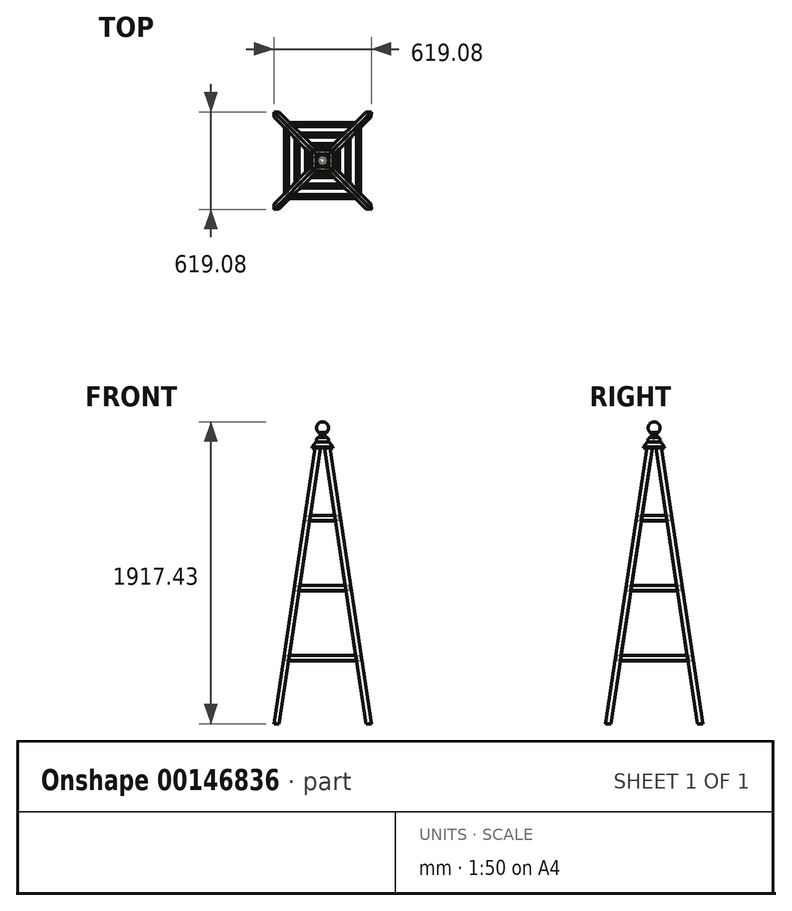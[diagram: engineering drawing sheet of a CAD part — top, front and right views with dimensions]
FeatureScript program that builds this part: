
annotation { "Feature Type Name" : "Feature", "Feature Type Description" : "" }
export const myFeature = defineFeature(function(context is Context, id is Id, definition is map)
    precondition{}
    {
        {
            assignVariable(context, id + "F0", {"name" : "Angle0", "anyValue" : 12 * degree});
        }
        {
            assignVariable(context, id + "F1", {"name" : "CentreSpread0", "anyValue" : 12});
        }
        {
            assignVariable(context, id + "F2", {"name" : "ArmOffset0", "anyValue" : ((((1800 - (sqrt(34 * 34 * 2) * sin(getVariable(context, 'Angle0')))) * sin(getVariable(context, 'Angle0')) + (sqrt(17 * 17 * 2) / cos(getVariable(context, 'Angle0')))) * sin(45 * degree)) + getVariable(context, 'CentreSpread0')) * mm});
        }
        {
            var Q0;
            Q0=qCreatedBy(makeId("Front.planeOp"),FACE);
            var sketch = newSketch(context, id + "F3", { "sketchPlane" : qUnion([Q0])});
            skLineSegment(sketch, "E0.bottom", {"start": v(-17, 900) * mm, "end": v(17, 900) * mm});
            skLineSegment(sketch, "E0.top", {"start": v(-17, -900) * mm, "end": v(17, -900) * mm});
            skLineSegment(sketch, "E0.left", {"start": v(-17, 900) * mm, "end": v(-17, -900) * mm});
            skLineSegment(sketch, "E0.right", {"start": v(17, 900) * mm, "end": v(17, -900) * mm});
            skPoint(sketch, "E0.middle", {"position": v(0, 0) * mm});
            skLineSegment(sketch, "E1", {"start": v(0, 0) * mm, "end": v(0, 406.37) * mm, "construction": true});
            skSolve(sketch);
        }
        {
            var Q0;
            Q0=sQuery(id+"F3.wireOp",EDGE,"E1");
            cPlane(context, id + "F4", {"entities" : qUnion([Q0]), "cplaneType" : CPlaneType.LINE_ANGLE, "offset" : 25 * mm, "angle" : 45 * degree, "width" : 150 * mm, "height" : 150 * mm});
        }
        {
            var Q0;
            Q0=sQuery(id+"F3.wireOp",EDGE,"E1");
            cPlane(context, id + "F5", {"entities" : qUnion([Q0]), "cplaneType" : CPlaneType.LINE_ANGLE, "offset" : 25 * mm, "angle" : 135 * degree, "width" : 150 * mm, "height" : 150 * mm});
        }
        {
            var Q0;
            Q0=qCreatedBy(id+"F5.planeOp",FACE);
            cPlane(context, id + "F6", {"entities" : qUnion([Q0]), "cplaneType" : CPlaneType.OFFSET, "offset" : (sqrt(17 * 17 * 2)) * mm, "oppositeDirection" : true, "width" : 150 * mm, "height" : 150 * mm});
        }
        {
            var Q0;
            Q0=qSketchRegion(id+"F3",true);
            extrude(context, id + "F7", {"entities" : qUnion([Q0]), "depth" : 17 * mm, "hasSecondDirection" : true, "secondDirectionOppositeDirection" : true, "secondDirectionDepth" : 17 * mm});
        }
        {
            var Q0;
            Q0=qCreatedBy(id+"F4.planeOp",FACE);
            var sketch = newSketch(context, id + "F8", { "sketchPlane" : qUnion([Q0])});
            skLineSegment(sketch, "E2", {"start": v(24.04, 900) * mm, "end": v(-24.04, 889.78) * mm});
            skLineSegment(sketch, "E3", {"start": v(-24.04, 900) * mm, "end": v(24.04, 900) * mm});
            skLineSegment(sketch, "E4", {"start": v(-24.04, 900) * mm, "end": v(-24.04, 889.78) * mm});
            skLineSegment(sketch, "E5", {"start": v(-24.04, -900) * mm, "end": v(24.04, -889.78) * mm});
            skLineSegment(sketch, "E6", {"start": v(-24.04, -900) * mm, "end": v(24.04, -900) * mm});
            skLineSegment(sketch, "E7", {"start": v(24.04, -900) * mm, "end": v(24.04, -889.78) * mm});
            skSolve(sketch);
        }
        {
            var Q0;
            Q0=qSketchRegion(id+"F8",true);
            extrude(context, id + "F9", {"entities" : qUnion([Q0]), "operationType" : NewBodyOperationType.REMOVE, "depth" : (sqrt(17 * 17 * 2)) * mm, "hasSecondDirection" : true, "secondDirectionOppositeDirection" : true, "secondDirectionDepth" : (sqrt(17 * 17 * 2)) * mm});
        }
        {
            var Q0;
            Q0=qCreatedBy(id+"F6.planeOp",FACE);
            var sketch = newSketch(context, id + "F10", { "sketchPlane" : qUnion([Q0])});
            skLineSegment(sketch, "E8", {"start": v(-24.04, -900) * mm, "end": v(24.04, -900) * mm, "construction": true});
            skSolve(sketch);
        }
        {
            var Q0;
            Q0=makeQuery(id+"F7.opExtrude","SWEPT_BODY",BODY,{"disambiguationData":[OSD([sQuery(id+"F3.wireOp",EDGE,"E0.bottom"),sQuery(id+"F3.wireOp",EDGE,"E0.top"),sQuery(id+"F3.wireOp",EDGE,"E0.left"),sQuery(id+"F3.wireOp",EDGE,"E0.right")])]});
            var Q1;
            Q1=sQuery(id+"F10.wireOp",EDGE,"E8");
            transform(context, id + "F11", {"entities" : qUnion([Q0]), "transformType" : TransformType.ROTATION, "transformAxis" : qUnion([Q1]), "angle" : getVariable(context, 'Angle0'), "makeCopy" : false});
        }
        {
            var Q0;
            Q0=makeQuery(id+"F7.opExtrude","SWEPT_BODY",BODY,{"disambiguationData":[OSD([sQuery(id+"F3.wireOp",EDGE,"E0.bottom"),sQuery(id+"F3.wireOp",EDGE,"E0.top"),sQuery(id+"F3.wireOp",EDGE,"E0.left"),sQuery(id+"F3.wireOp",EDGE,"E0.right")])]});
            transform(context, id + "F12", {"entities" : qUnion([Q0]), "transformType" : TransformType.TRANSLATION_3D, "dx" : getVariable(context, 'ArmOffset0'), "dy" : -getVariable(context, 'ArmOffset0'), "dz" : 0 * mm, "makeCopy" : false});
        }
        {
            var Q0;
            Q0=makeQuery(id+"F7.opExtrude","SWEPT_BODY",BODY,{"disambiguationData":[OSD([sQuery(id+"F3.wireOp",EDGE,"E0.bottom"),sQuery(id+"F3.wireOp",EDGE,"E0.top"),sQuery(id+"F3.wireOp",EDGE,"E0.left"),sQuery(id+"F3.wireOp",EDGE,"E0.right")])]});
            var Q1;
            Q1=sQuery(id+"F3.wireOp",EDGE,"E1");
            circularPattern(context, id + "F13", {"entities" : qUnion([Q0]), "axis" : qUnion([Q1]), "angle" : 360 * degree, "instanceCount" : 4, "equalSpace" : true});
        }
        {
            var Q0;
            Q0=qCreatedBy(makeId("Top.planeOp"),FACE);
            var sketch = newSketch(context, id + "F14", { "sketchPlane" : qUnion([Q0])});
            skLineSegment(sketch, "E9.bottom", {"start": v(67, 67) * mm, "end": v(-67, 67) * mm});
            skLineSegment(sketch, "E9.top", {"start": v(67, -67) * mm, "end": v(-67, -67) * mm});
            skLineSegment(sketch, "E9.left", {"start": v(67, 67) * mm, "end": v(67, -67) * mm});
            skLineSegment(sketch, "E9.right", {"start": v(-67, 67) * mm, "end": v(-67, -67) * mm});
            skPoint(sketch, "E9.middle", {"position": v(0, 0) * mm});
            skSolve(sketch);
        }
        {
            var Q0;
            Q0=qSketchRegion(id+"F14",true);
            extrude(context, id + "F15", {"entities" : qUnion([Q0]), "depth" : 32 * mm, "hasDraft" : true, "draftAngle" : 38 * degree, "draftPullDirection" : true, "hasSecondDirection" : true, "secondDirectionOppositeDirection" : true, "secondDirectionDepth" : 8 * mm});
        }
        {
            var Q0;
            Q0=makeQuery(id+"F15.split0.splitOp","SPLIT",BODY,{"derivedFrom":makeQuery(id+"F15.opExtrude","SWEPT_BODY",BODY,{"disambiguationData":[OSD([sQuery(id+"F14.wireOp",EDGE,"E9.bottom"),sQuery(id+"F14.wireOp",EDGE,"E9.top"),sQuery(id+"F14.wireOp",EDGE,"E9.left"),sQuery(id+"F14.wireOp",EDGE,"E9.right")])]})});
            transform(context, id + "F16", {"entities" : qUnion([Q0]), "transformType" : TransformType.TRANSLATION_3D, "dx" : 0 * mm, "dy" : 0 * mm, "dz" : ((1800 * cos(getVariable(context, 'Angle0')) - (tan(getVariable(context, 'Angle0')) * sqrt(34 * 34 * 2)) - 892)) * mm, "makeCopy" : false});
        }
        {
            var Q0;
            Q0=qCreatedBy(makeId("Front.planeOp"),FACE);
            var sketch = newSketch(context, id + "F17", { "sketchPlane" : qUnion([Q0])});
            skLineSegment(sketch, "E10", {"start": v(0, 0) * mm, "end": v(33, 0) * mm});
            skFitSpline(sketch, "E11", {"points": [v(33, 0) * mm, v(38, 16.22) * mm, v(26, 28) * mm], "startDerivative": vector(25.56, 0) * mm, "endDerivative": vector(-18.97, 0) * mm});
            skLineSegment(sketch, "E12", {"start": v(26, 28) * mm, "end": v(26, 33) * mm});
            skFitSpline(sketch, "E13", {"points": [v(26, 33) * mm, v(13.8, 42.6) * mm, v(22, 53) * mm], "startDerivative": vector(-39.34, 1.43) * mm, "endDerivative": vector(35.56, 0.88) * mm});
            skLineSegment(sketch, "E14", {"start": v(22, 53) * mm, "end": v(22, 58) * mm});
            skArc(sketch, "E15", {"start": v(22, 58) * mm, "mid": v(36.2, 100.53) * mm, "end": v(0, 126.98) * mm});
            skLineSegment(sketch, "E16", {"start": v(0, 0) * mm, "end": v(0, 126.98) * mm});
            skSolve(sketch);
        }
        {
            var Q0;
            Q0=makeQuery(id+"F17.imprint","IMPRINT",FACE,{"disambiguationData":[TD([[makeQuery(id+"F17.imprint","IMPRINT",EDGE,{"derivedFrom":sQuery(id+"F17.wireOp",EDGE,"E10")}),1.0]])]});
            var Q1;
            Q1=sQuery(id+"F17.wireOp",EDGE,"E16");
            revolve(context, id + "F18", {"entities" : qUnion([Q0]), "axis" : qUnion([Q1]), "revolveType" : RevolveType.FULL});
        }
        {
            var Q0;
            Q0=makeQuery(id+"F18.opRevolve","SWEPT_BODY",BODY,{"disambiguationData":[OSD([sQuery(id+"F17.wireOp",EDGE,"E10"),sQuery(id+"F17.wireOp",EDGE,"E11"),sQuery(id+"F17.wireOp",EDGE,"E12"),sQuery(id+"F17.wireOp",EDGE,"E13"),sQuery(id+"F17.wireOp",EDGE,"E14"),sQuery(id+"F17.wireOp",EDGE,"E15"),sQuery(id+"F17.wireOp",EDGE,"E16")])]});
            transform(context, id + "F19", {"entities" : qUnion([Q0]), "transformType" : TransformType.TRANSLATION_3D, "dx" : 0 * mm, "dy" : 0 * mm, "dz" : ((1800 * cos(getVariable(context, 'Angle0')) - (tan(getVariable(context, 'Angle0')) * sqrt(34 * 34 * 2)) - 860)) * mm, "makeCopy" : false});
        }
        {
            var Q0;
            Q0=qCreatedBy(makeId("Front.planeOp"),FACE);
            var sketch = newSketch(context, id + "F20", { "sketchPlane" : qUnion([Q0])});
            skLineSegment(sketch, "E17", {"start": v(0, -900) * mm, "end": v(0, 850.45) * mm, "construction": true});
            skLineSegment(sketch, "E18", {"start": v(-29.38, 850.45) * mm, "end": v(-29.38, -900) * mm, "construction": true});
            skLineSegment(sketch, "E19", {"start": v(-29.38, 850.45) * mm, "end": v(-228.58, -484.78) * mm, "construction": true});
            skLineSegment(sketch, "E20.bottom", {"start": v(-216.82, -470.35) * mm, "end": v(-235.61, -467.55) * mm});
            skLineSegment(sketch, "E20.top", {"start": v(-221.54, -502) * mm, "end": v(-240.34, -499.2) * mm});
            skLineSegment(sketch, "E20.left", {"start": v(-216.82, -470.35) * mm, "end": v(-221.54, -502) * mm});
            skLineSegment(sketch, "E20.right", {"start": v(-235.61, -467.55) * mm, "end": v(-240.34, -499.2) * mm});
            skPoint(sketch, "E20.middle", {"position": v(-228.58, -484.78) * mm});
            skLineSegment(sketch, "E21.bottom", {"start": v(-173.94, -54.13) * mm, "end": v(-155.14, -56.93) * mm});
            skLineSegment(sketch, "E21.top", {"start": v(-169.21, -22.48) * mm, "end": v(-150.42, -25.28) * mm});
            skLineSegment(sketch, "E21.left", {"start": v(-173.94, -54.13) * mm, "end": v(-169.21, -22.48) * mm});
            skLineSegment(sketch, "E21.right", {"start": v(-155.14, -56.93) * mm, "end": v(-150.42, -25.28) * mm});
            skPoint(sketch, "E21.middle", {"position": v(-162.18, -39.7) * mm});
            skLineSegment(sketch, "E22.bottom", {"start": v(-107.54, 390.95) * mm, "end": v(-88.74, 388.14) * mm});
            skLineSegment(sketch, "E22.top", {"start": v(-102.81, 422.6) * mm, "end": v(-84.02, 419.8) * mm});
            skLineSegment(sketch, "E22.left", {"start": v(-107.54, 390.95) * mm, "end": v(-102.81, 422.6) * mm});
            skLineSegment(sketch, "E22.right", {"start": v(-88.74, 388.14) * mm, "end": v(-84.02, 419.8) * mm});
            skPoint(sketch, "E22.middle", {"position": v(-95.78, 405.37) * mm});
            skLineSegment(sketch, "E23.MirrorCS", {"start": v(88.74, 388.14) * mm, "end": v(84.02, 419.8) * mm});
            skLineSegment(sketch, "E24.MirrorCS", {"start": v(107.54, 390.95) * mm, "end": v(88.74, 388.14) * mm});
            skLineSegment(sketch, "E25.MirrorCS", {"start": v(107.54, 390.95) * mm, "end": v(102.81, 422.6) * mm});
            skLineSegment(sketch, "E26.MirrorCS", {"start": v(102.81, 422.6) * mm, "end": v(84.02, 419.8) * mm});
            skLineSegment(sketch, "E27.MirrorCS", {"start": v(169.21, -22.48) * mm, "end": v(150.42, -25.28) * mm});
            skLineSegment(sketch, "E28.MirrorCS", {"start": v(155.14, -56.93) * mm, "end": v(150.42, -25.28) * mm});
            skLineSegment(sketch, "E29.MirrorCS", {"start": v(173.94, -54.13) * mm, "end": v(155.14, -56.93) * mm});
            skLineSegment(sketch, "E30.MirrorCS", {"start": v(173.94, -54.13) * mm, "end": v(169.21, -22.48) * mm});
            skLineSegment(sketch, "E31.MirrorCS", {"start": v(216.82, -470.35) * mm, "end": v(235.61, -467.55) * mm});
            skLineSegment(sketch, "E32.MirrorCS", {"start": v(216.82, -470.35) * mm, "end": v(221.54, -502) * mm});
            skLineSegment(sketch, "E33.MirrorCS", {"start": v(221.54, -502) * mm, "end": v(240.34, -499.2) * mm});
            skLineSegment(sketch, "E34.MirrorCS", {"start": v(235.61, -467.55) * mm, "end": v(240.34, -499.2) * mm});
            skSolve(sketch);
        }
        {
            var Q0;
            Q0 = qSketchRegion(id + "F20", true);
            extrude(context, id + "F21", {"entities" : qUnion([Q0]), "endBound" : BoundingType.UP_TO_NEXT, "depth" : 25 * mm, "hasSecondDirection" : true, "secondDirectionBound" : SecondDirectionBoundingType.UP_TO_NEXT, "secondDirectionOppositeDirection" : true, "secondDirectionDepth" : 25 * mm});
        }
        {
            var Q0;
            Q0=makeQuery(id+"F21.opExtrude","SWEPT_BODY",BODY,{"disambiguationData":[OSD([sQuery(id+"F20.wireOp",EDGE,"E20.bottom"),sQuery(id+"F20.wireOp",EDGE,"E20.top"),sQuery(id+"F20.wireOp",EDGE,"E20.left"),sQuery(id+"F20.wireOp",EDGE,"E20.right")])]});
            var Q1;
            Q1=makeQuery(id+"F21.opExtrude","SWEPT_BODY",BODY,{"disambiguationData":[OSD([sQuery(id+"F20.wireOp",EDGE,"E21.bottom"),sQuery(id+"F20.wireOp",EDGE,"E21.top"),sQuery(id+"F20.wireOp",EDGE,"E21.left"),sQuery(id+"F20.wireOp",EDGE,"E21.right")])]});
            var Q2;
            Q2=makeQuery(id+"F21.opExtrude","SWEPT_BODY",BODY,{"disambiguationData":[OSD([sQuery(id+"F20.wireOp",EDGE,"E22.bottom"),sQuery(id+"F20.wireOp",EDGE,"E22.top"),sQuery(id+"F20.wireOp",EDGE,"E22.left"),sQuery(id+"F20.wireOp",EDGE,"E22.right")])]});
            var Q3;
            Q3=makeQuery(id+"F21.opExtrude","SWEPT_BODY",BODY,{"disambiguationData":[OSD([sQuery(id+"F20.wireOp",EDGE,"E23.MirrorCS"),sQuery(id+"F20.wireOp",EDGE,"E24.MirrorCS"),sQuery(id+"F20.wireOp",EDGE,"E25.MirrorCS"),sQuery(id+"F20.wireOp",EDGE,"E26.MirrorCS")])]});
            var Q4;
            Q4=makeQuery(id+"F21.opExtrude","SWEPT_BODY",BODY,{"disambiguationData":[OSD([sQuery(id+"F20.wireOp",EDGE,"E28.MirrorCS"),sQuery(id+"F20.wireOp",EDGE,"E29.MirrorCS"),sQuery(id+"F20.wireOp",EDGE,"E30.MirrorCS"),sQuery(id+"F20.wireOp",EDGE,"E27.MirrorCS")])]});
            var Q5;
            Q5=makeQuery(id+"F21.opExtrude","SWEPT_BODY",BODY,{"disambiguationData":[OSD([sQuery(id+"F20.wireOp",EDGE,"E32.MirrorCS"),sQuery(id+"F20.wireOp",EDGE,"E33.MirrorCS"),sQuery(id+"F20.wireOp",EDGE,"E34.MirrorCS"),sQuery(id+"F20.wireOp",EDGE,"E31.MirrorCS")])]});
            var Q6;
            Q6=sQuery(id+"F20.wireOp",EDGE,"E17");
            transform(context, id + "F22", {"entities" : qUnion([Q0, Q1, Q2, Q3, Q4, Q5]), "transformType" : TransformType.ROTATION, "transformAxis" : qUnion([Q6]), "angle" : 90 * degree, "makeCopy" : true});
        }
    });
